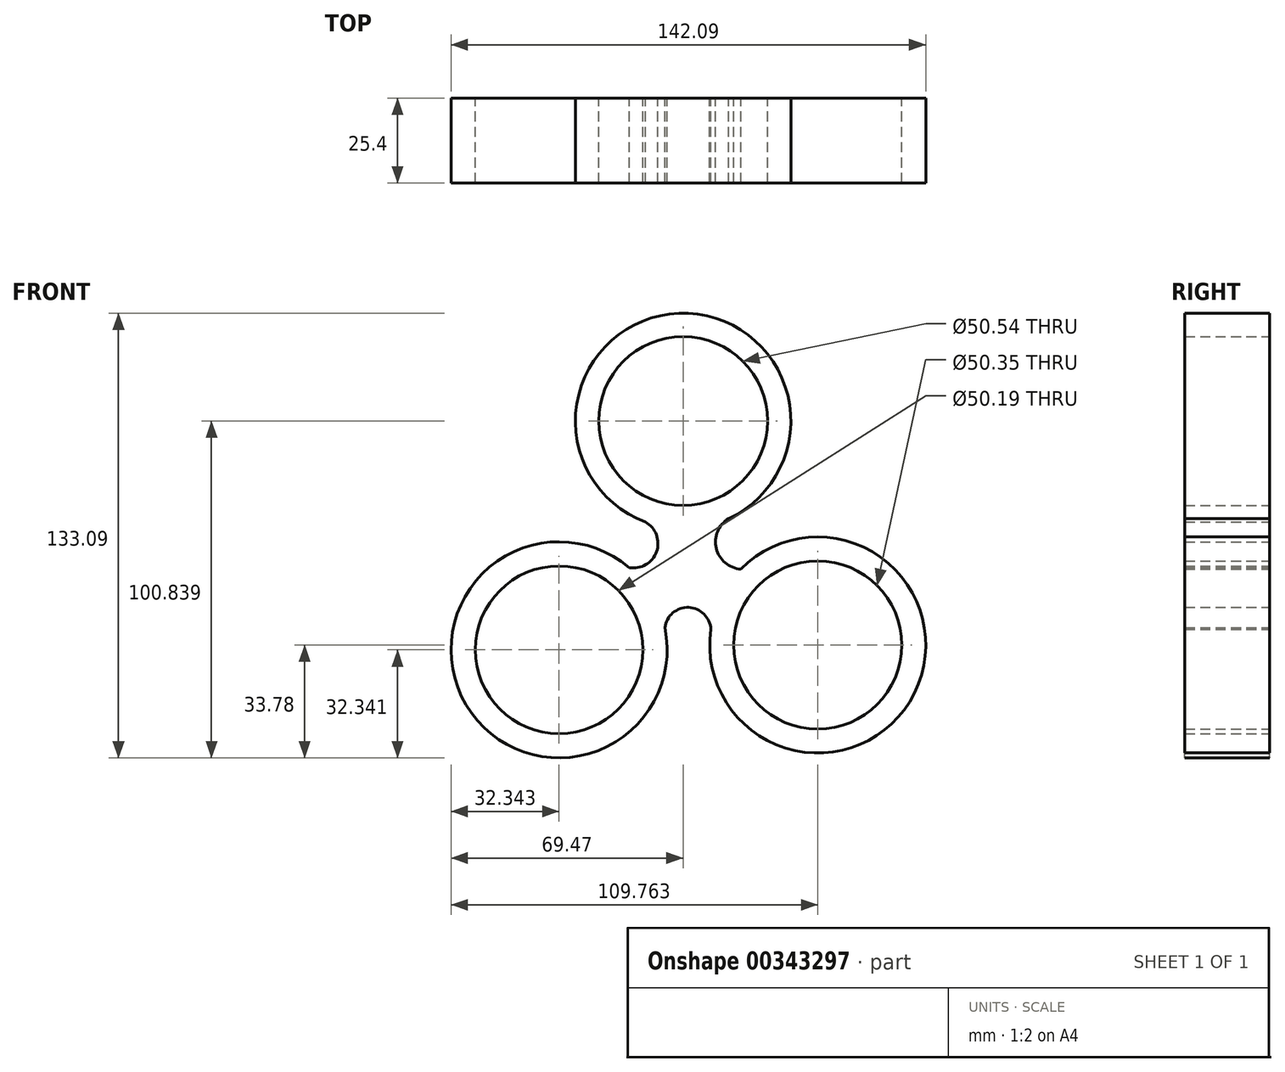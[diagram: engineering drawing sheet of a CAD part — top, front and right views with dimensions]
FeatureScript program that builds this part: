
annotation { "Feature Type Name" : "Feature", "Feature Type Description" : "" }
export const myFeature = defineFeature(function(context is Context, id is Id, definition is map)
    precondition{}
    {
        {
            var Q0;
            Q0=qCreatedBy(makeId("Front.planeOp"),FACE);
            var sketch = newSketch(context, id + "F0", { "sketchPlane" : qUnion([Q0])});
            skCircle(sketch, "E0", {"center": v(0, 31.66) * mm, "radius": 32.25 * mm});
            skCircle(sketch, "E1", {"center": v(-37.13, -36.84) * mm, "radius": 32.34 * mm});
            skCircle(sketch, "E2", {"center": v(40.3, -35.4) * mm, "radius": 32.33 * mm});
            skCircle(sketch, "E3", {"center": v(0, 31.66) * mm, "radius": 25.27 * mm});
            skCircle(sketch, "E4", {"center": v(-37.13, -36.84) * mm, "radius": 25.1 * mm});
            skCircle(sketch, "E5", {"center": v(40.3, -35.4) * mm, "radius": 25.17 * mm});
            skArc(sketch, "E6", {"start": v(-21.3, -8.64) * mm, "mid": v(-9.06, -9.47) * mm, "end": v(-13.02, 2.15) * mm});
            skArc(sketch, "E7", {"start": v(8.3, -30.75) * mm, "mid": v(1.66, -24.16) * mm, "end": v(-5.47, -30.22) * mm});
            skArc(sketch, "E8", {"start": v(14.88, 3.04) * mm, "mid": v(9.76, -5.79) * mm, "end": v(17.3, -12.68) * mm});
            skSolve(sketch);
        }
        {
            var Q0;
            Q0 = qSketchRegion(id + "F0", true);
            extrude(context, id + "F1", {"entities" : qUnion([Q0]), "depth" : 11.18 * mm});
        }
        {
            var Q0;
            Q0 = qSketchRegion(id + "F0", true);
            extrude(context, id + "F2", {"entities" : qUnion([Q0]), "operationType" : NewBodyOperationType.ADD, "depth" : 25.4 * mm});
        }
    });
